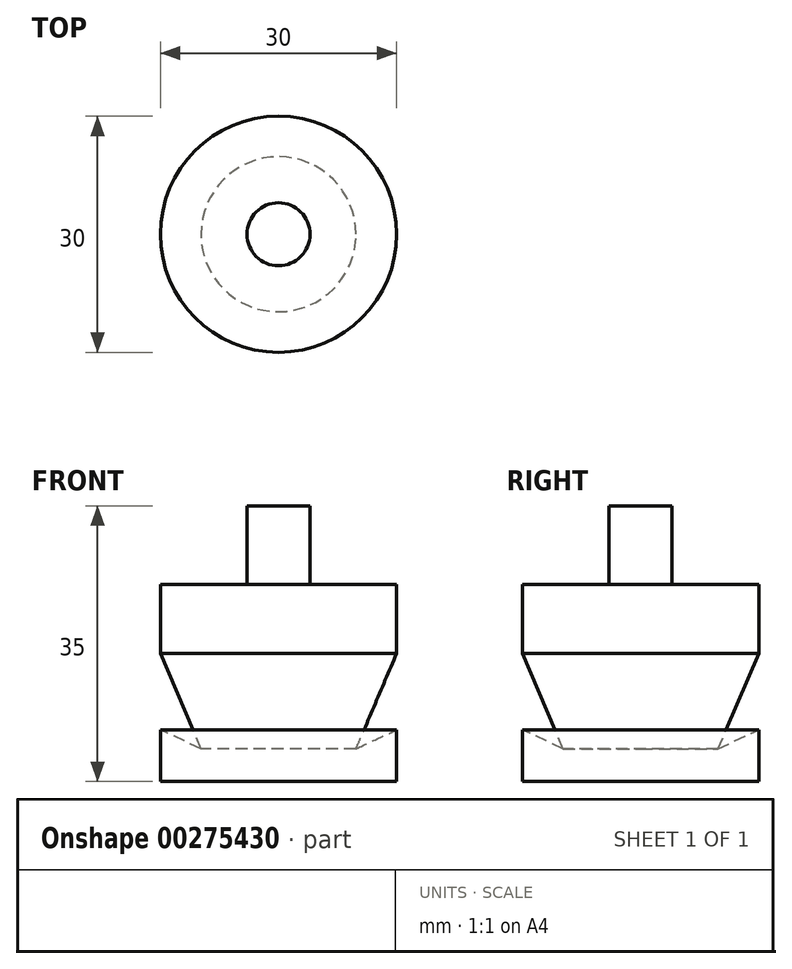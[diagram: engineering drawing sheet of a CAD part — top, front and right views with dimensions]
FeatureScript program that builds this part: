
annotation { "Feature Type Name" : "Feature", "Feature Type Description" : "" }
export const myFeature = defineFeature(function(context is Context, id is Id, definition is map)
    precondition{}
    {
        {
            var Q0;
            Q0=qCreatedBy(makeId("Front.planeOp"),FACE);
            var sketch = newSketch(context, id + "F0", { "sketchPlane" : qUnion([Q0])});
            skLineSegment(sketch, "E0", {"start": v(0, 25) * mm, "end": v(0, 0) * mm});
            skLineSegment(sketch, "E1", {"start": v(0, 25) * mm, "end": v(-15, 25) * mm});
            skLineSegment(sketch, "E2", {"start": v(-15, 0) * mm, "end": v(0, 0) * mm});
            skLineSegment(sketch, "E3", {"start": v(-15, 16.25) * mm, "end": v(-9.84, 4.15) * mm});
            skPoint(sketch, "E3.endSnap0", {"position": v(-15, 4.15) * mm});
            skLineSegment(sketch, "E4", {"start": v(-9.84, 4.15) * mm, "end": v(-15, 6.52) * mm});
            skLineSegment(sketch, "E5", {"start": v(-15, 16.25) * mm, "end": v(-15, 25) * mm});
            skLineSegment(sketch, "E6", {"start": v(-15, 6.52) * mm, "end": v(-15, 0) * mm});
            skSolve(sketch);
        }
        {
            var Q0;
            Q0 = qSketchRegion(id + "F0", true);
            var Q1;
            Q1=sQuery(id+"F0.wireOp",EDGE,"E0");
            revolve(context, id + "F1", {"entities" : qUnion([Q0]), "axis" : qUnion([Q1]), "revolveType" : RevolveType.FULL});
        }
        {
            var Q0;
            Q0=makeQuery(id+"F1.opRevolve","SWEPT_FACE",FACE,{"disambiguationData":[OSD([sQuery(id+"F0.wireOp",EDGE,"E1")])]});
            var sketch = newSketch(context, id + "F2", { "sketchPlane" : qUnion([Q0])});
            skCircle(sketch, "E7", {"center": v(0, 0) * mm, "radius": 4 * mm});
            skSolve(sketch);
        }
        {
            var Q0;
            Q0 = qSketchRegion(id + "F2", true);
            extrude(context, id + "F3", {"entities" : qUnion([Q0]), "operationType" : NewBodyOperationType.ADD, "depth" : 10 * mm});
        }
    });
